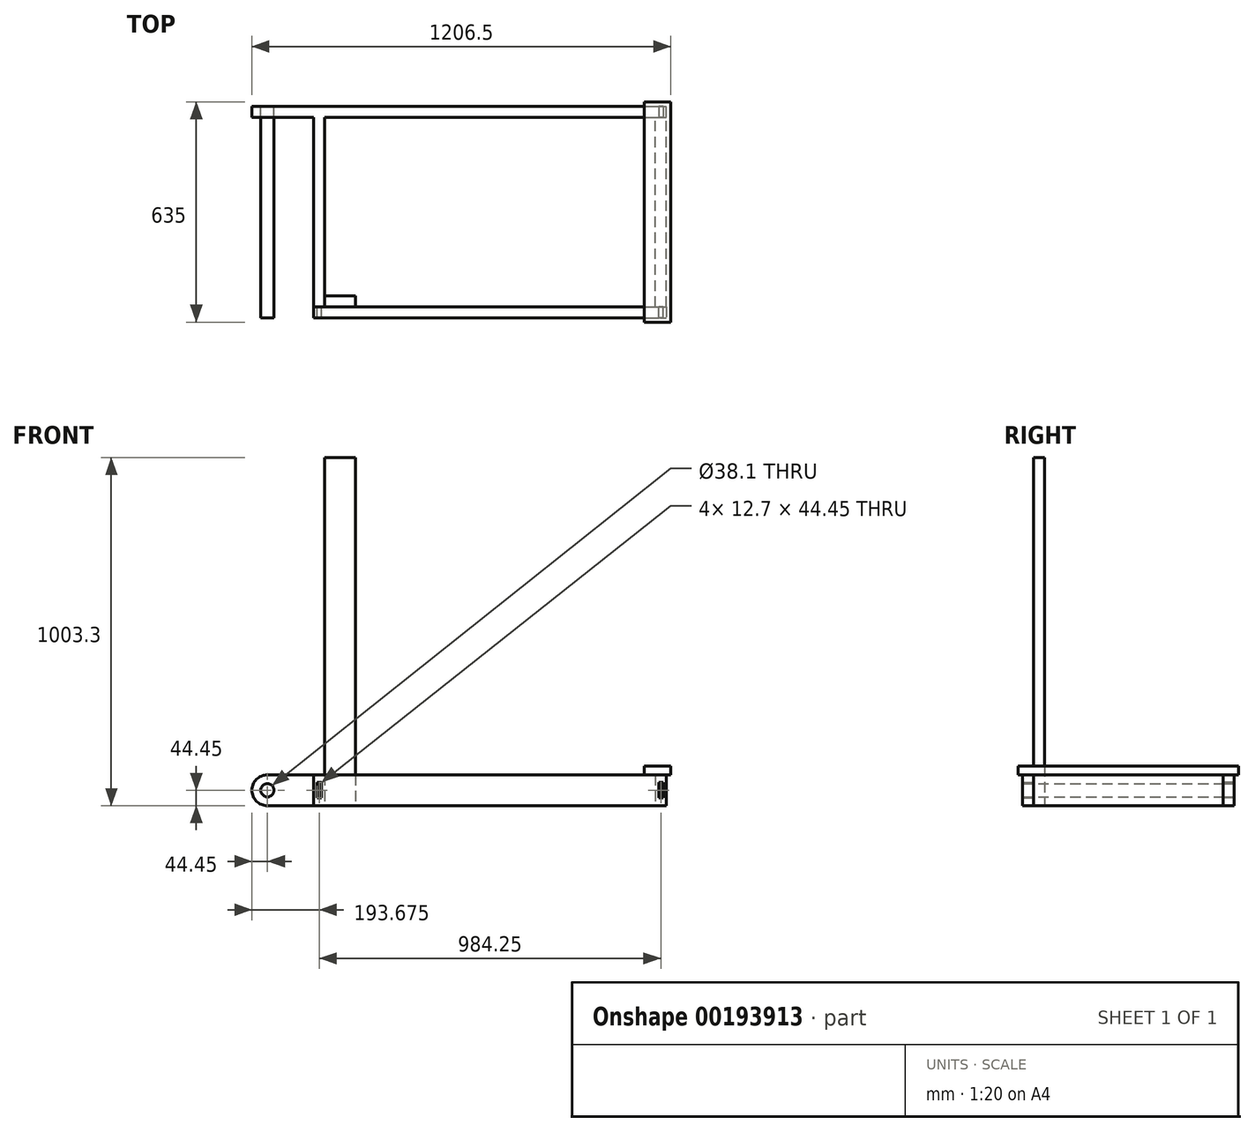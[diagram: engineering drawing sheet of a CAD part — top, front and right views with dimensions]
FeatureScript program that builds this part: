
annotation { "Feature Type Name" : "Feature", "Feature Type Description" : "" }
export const myFeature = defineFeature(function(context is Context, id is Id, definition is map)
    precondition{}
    {
        {
            var Q0;
            Q0=qCreatedBy(makeId("Top.planeOp"),FACE);
            var sketch = newSketch(context, id + "F0", { "sketchPlane" : qUnion([Q0])});
            skLineSegment(sketch, "E0.bottom", {"start": v(-508, 304.8) * mm, "end": v(508, 304.8) * mm});
            skLineSegment(sketch, "E0.top", {"start": v(-508, -304.8) * mm, "end": v(508, -304.8) * mm});
            skLineSegment(sketch, "E0.left", {"start": v(-508, 304.8) * mm, "end": v(-508, -304.8) * mm});
            skLineSegment(sketch, "E0.right", {"start": v(508, 304.8) * mm, "end": v(508, -304.8) * mm});
            skPoint(sketch, "E0.middle", {"position": v(0, 0) * mm});
            skLineSegment(sketch, "E1.0", {"start": v(-508, -273.05) * mm, "end": v(508, -273.05) * mm});
            skLineSegment(sketch, "E1.1", {"start": v(-476.25, 304.8) * mm, "end": v(-476.25, -304.8) * mm});
            skLineSegment(sketch, "E1.2", {"start": v(-508, 273.05) * mm, "end": v(508, 273.05) * mm});
            skLineSegment(sketch, "E1.3", {"start": v(476.25, 304.8) * mm, "end": v(476.25, -304.8) * mm});
            skSolve(sketch);
        }
        {
            var Q0;
            {var subQ4=sQuery(id+"F0.wireOp",EDGE,"E0.top");Q0=makeQuery(id+"F0.imprint","IMPRINT",FACE,{"disambiguationData":[TD([[makeQuery(id+"F0.imprint","IMPRINT",EDGE,{"derivedFrom":subQ4}),1.0]])]});}
            extrude(context, id + "F1", {"entities" : qUnion([Q0]), "oppositeDirection" : true, "depth" : 88.9 * mm});
        }
        {
            var Q0;
            Q0=makeQuery(id+"F1.opExtrude","SWEPT_FACE",FACE,{"disambiguationData":[OSD([sQuery(id+"F0.wireOp",EDGE,"E1.0")])]});
            var sketch = newSketch(context, id + "F2", { "sketchPlane" : qUnion([Q0])});
            skLineSegment(sketch, "E2", {"start": v(-476.25, 0) * mm, "end": v(-476.25, -88.9) * mm, "construction": true});
            skLineSegment(sketch, "E3", {"start": v(-476.25, 0) * mm, "end": v(-508, -88.9) * mm, "construction": true});
            skLineSegment(sketch, "E4.bottom", {"start": v(-498.47, -22.23) * mm, "end": v(-485.77, -22.23) * mm});
            skLineSegment(sketch, "E4.top", {"start": v(-498.47, -66.68) * mm, "end": v(-485.77, -66.68) * mm});
            skLineSegment(sketch, "E4.left", {"start": v(-498.47, -22.23) * mm, "end": v(-498.47, -66.68) * mm});
            skLineSegment(sketch, "E4.right", {"start": v(-485.77, -22.23) * mm, "end": v(-485.77, -66.68) * mm});
            skPoint(sketch, "E4.middle", {"position": v(-492.12, -44.45) * mm});
            skLineSegment(sketch, "E5", {"start": v(0, 0) * mm, "end": v(0, -88.9) * mm, "construction": true});
            skLineSegment(sketch, "E6.MirrorCS", {"start": v(485.77, -22.22) * mm, "end": v(485.77, -66.67) * mm});
            skLineSegment(sketch, "E7.MirrorCS", {"start": v(498.47, -22.22) * mm, "end": v(498.47, -66.67) * mm});
            skLineSegment(sketch, "E8.MirrorCS", {"start": v(498.47, -22.22) * mm, "end": v(485.77, -22.22) * mm});
            skLineSegment(sketch, "E9.MirrorCS", {"start": v(498.47, -66.67) * mm, "end": v(485.77, -66.67) * mm});
            skSolve(sketch);
        }
        {
            var Q0;
            Q0=makeQuery(id+"F2.imprint","IMPRINT",FACE,{"disambiguationData":[TD([[makeQuery(id+"F2.imprint","IMPRINT",EDGE,{"derivedFrom":sQuery(id+"F2.wireOp",EDGE,"E4.bottom")}),-1.0]])]});
            var Q1;
            Q1=makeQuery(id+"F2.imprint","IMPRINT",FACE,{"disambiguationData":[TD([[makeQuery(id+"F2.imprint","IMPRINT",EDGE,{"derivedFrom":sQuery(id+"F2.wireOp",EDGE,"E6.MirrorCS")}),1.0]])]});
            extrude(context, id + "F3", {"entities" : qUnion([Q0, Q1]), "operationType" : NewBodyOperationType.REMOVE, "endBound" : BoundingType.UP_TO_NEXT, "oppositeDirection" : true, "depth" : 25.4 * mm});
        }
        {
            var Q0;
            Q0=makeQuery(id+"F1.opExtrude","SWEPT_BODY",BODY,{"disambiguationData":[OSD([sQuery(id+"F0.wireOp",EDGE,"E0.top"),sQuery(id+"F0.wireOp",EDGE,"E0.left"),sQuery(id+"F0.wireOp",EDGE,"E0.right"),sQuery(id+"F0.wireOp",EDGE,"E1.0")])]});
            var Q1;
            Q1=qCreatedBy(makeId("Front.planeOp"),FACE);
            mirror(context, id + "F4", {"entities" : qUnion([Q0]), "mirrorPlane" : qUnion([Q1])});
        }
        {
            var Q0;
            {var subQ0=sQuery(id+"F0.wireOp",EDGE,"E0.right");var subQ1=sQuery(id+"F0.wireOp",EDGE,"E0.bottom");var subQ2=makeQuery(id+"F0.imprint","INTERSECT",VERTEX,{"derivedFrom":[subQ1,subQ0]});Q0=makeQuery(id+"F0.imprint","IMPRINT",FACE,{"disambiguationData":[TD([[makeQuery(id+"F0.imprint","IMPRINT",EDGE,{"disambiguationData":[TD([[subQ2,1.0]])],"derivedFrom":subQ1}),-1.0]])]});}
            var Q1;
            {var subQ0=sQuery(id+"F0.wireOp",EDGE,"E1.0");var subQ1=sQuery(id+"F0.wireOp",EDGE,"E0.right");var subQ2=makeQuery(id+"F0.imprint","INTERSECT",VERTEX,{"derivedFrom":[subQ1,subQ0]});Q1=makeQuery(id+"F0.imprint","IMPRINT",FACE,{"disambiguationData":[TD([[makeQuery(id+"F0.imprint","IMPRINT",EDGE,{"disambiguationData":[TD([[subQ2,1.0]])],"derivedFrom":subQ1}),-1.0]])]});}
            var Q2;
            {var subQ0=sQuery(id+"F0.wireOp",EDGE,"E0.right");var subQ1=sQuery(id+"F0.wireOp",EDGE,"E0.top");var subQ2=makeQuery(id+"F0.imprint","INTERSECT",VERTEX,{"derivedFrom":[subQ1,subQ0]});Q2=makeQuery(id+"F0.imprint","IMPRINT",FACE,{"disambiguationData":[TD([[makeQuery(id+"F0.imprint","IMPRINT",EDGE,{"disambiguationData":[TD([[subQ2,1.0]])],"derivedFrom":subQ1}),1.0]])]});}
            var Q3;
            Q3=makeQuery(id+"F1.opExtrude","CAP_FACE",FACE,{"disambiguationData":[OSD([sQuery(id+"F0.wireOp",EDGE,"E0.top"),sQuery(id+"F0.wireOp",EDGE,"E0.left"),sQuery(id+"F0.wireOp",EDGE,"E0.right"),sQuery(id+"F0.wireOp",EDGE,"E1.0")])],"isStart":false});
            extrude(context, id + "F5", {"entities" : qUnion([Q0, Q1, Q2]), "endBound" : BoundingType.UP_TO_SURFACE, "oppositeDirection" : true, "endBoundEntityFace" : qUnion([Q3]), "depth" : 25.4 * mm});
        }
        {
            var Q0;
            Q0=makeQuery(id+"F1.opExtrude","SWEPT_BODY",BODY,{"disambiguationData":[OSD([sQuery(id+"F0.wireOp",EDGE,"E0.top"),sQuery(id+"F0.wireOp",EDGE,"E0.left"),sQuery(id+"F0.wireOp",EDGE,"E0.right"),sQuery(id+"F0.wireOp",EDGE,"E1.0")])]});
            var Q1;
            Q1=makeQuery(id+"F4.opPattern","COPY",BODY,{"derivedFrom":makeQuery(id+"F1.opExtrude","SWEPT_BODY",BODY,{"disambiguationData":[OSD([sQuery(id+"F0.wireOp",EDGE,"E0.top"),sQuery(id+"F0.wireOp",EDGE,"E0.left"),sQuery(id+"F0.wireOp",EDGE,"E0.right"),sQuery(id+"F0.wireOp",EDGE,"E1.0")])]}),"instanceName":"1"});
            var Q2;
            Q2=makeQuery(id+"F5.opExtrude","SWEPT_BODY",BODY,{"disambiguationData":[OSD([sQuery(id+"F0.wireOp",EDGE,"E0.bottom"),sQuery(id+"F0.wireOp",EDGE,"E0.top"),sQuery(id+"F0.wireOp",EDGE,"E0.right"),sQuery(id+"F0.wireOp",EDGE,"E1.3")])]});
            booleanBodies(context, id + "F6", {"operationType" : BooleanOperationType.SUBTRACTION, "tools" : qUnion([Q0, Q1]), "targets" : qUnion([Q2]), "keepTools" : true});
        }
        {
            var Q0;
            Q0=makeQuery(id+"F5.opExtrude","SWEPT_BODY",BODY,{"disambiguationData":[OSD([sQuery(id+"F0.wireOp",EDGE,"E0.bottom"),sQuery(id+"F0.wireOp",EDGE,"E0.top"),sQuery(id+"F0.wireOp",EDGE,"E0.right"),sQuery(id+"F0.wireOp",EDGE,"E1.3")])]});
            var Q1;
            Q1=qCreatedBy(makeId("Right.planeOp"),FACE);
            mirror(context, id + "F7", {"entities" : qUnion([Q0]), "mirrorPlane" : qUnion([Q1])});
        }
        {
            var Q0;
            {var subQ0=sQuery(id+"F0.wireOp",EDGE,"E0.left");var subQ1=sQuery(id+"F0.wireOp",EDGE,"E0.top");var subQ2=makeQuery(id+"F0.imprint","INTERSECT",VERTEX,{"derivedFrom":[subQ1,subQ0]});Q0=makeQuery(id+"F0.imprint","IMPRINT",FACE,{"disambiguationData":[TD([[makeQuery(id+"F0.imprint","IMPRINT",EDGE,{"disambiguationData":[TD([[subQ2,-1.0]])],"derivedFrom":subQ1}),1.0]])]});}
            var sketch = newSketch(context, id + "F8", { "sketchPlane" : qUnion([Q0])});
            skLineSegment(sketch, "E10.0", {"start": v(-476.25, 304.8) * mm, "end": v(-476.25, -304.8) * mm, "construction": true});
            skLineSegment(sketch, "E11.0", {"start": v(-508, -273.05) * mm, "end": v(508, -273.05) * mm, "construction": true});
            skLineSegment(sketch, "E12.bottom", {"start": v(-476.25, -273.05) * mm, "end": v(-387.35, -273.05) * mm});
            skLineSegment(sketch, "E12.top", {"start": v(-476.25, -241.3) * mm, "end": v(-387.35, -241.3) * mm});
            skLineSegment(sketch, "E12.left", {"start": v(-476.25, -273.05) * mm, "end": v(-476.25, -241.3) * mm});
            skLineSegment(sketch, "E12.right", {"start": v(-387.35, -273.05) * mm, "end": v(-387.35, -241.3) * mm});
            skSolve(sketch);
        }
        {
            var Q0;
            Q0 = qSketchRegion(id + "F8", true);
            var Q1;
            Q1=makeQuery(id+"F1.opExtrude","CAP_FACE",FACE,{"disambiguationData":[OSD([sQuery(id+"F0.wireOp",EDGE,"E0.top"),sQuery(id+"F0.wireOp",EDGE,"E0.left"),sQuery(id+"F0.wireOp",EDGE,"E0.right"),sQuery(id+"F0.wireOp",EDGE,"E1.0")])],"isStart":false});
            extrude(context, id + "F9", {"entities" : qUnion([Q0]), "depth" : 914.4 * mm, "hasSecondDirection" : true, "secondDirectionBound" : SecondDirectionBoundingType.UP_TO_SURFACE, "secondDirectionOppositeDirection" : true, "secondDirectionBoundEntityFace" : qUnion([Q1]), "secondDirectionDepth" : 25.4 * mm});
        }
        {
            var Q0;
            Q0=makeQuery(id+"F4.opPattern","COPY",FACE,{"derivedFrom":makeQuery(id+"F1.opExtrude","SWEPT_FACE",FACE,{"disambiguationData":[OSD([sQuery(id+"F0.wireOp",EDGE,"E0.left")])]}),"instanceName":"1"});
            var sketch = newSketch(context, id + "F10", { "sketchPlane" : qUnion([Q0])});
            skLineSegment(sketch, "E13.0.0", {"start": v(-273.05, 0) * mm, "end": v(-304.8, 0) * mm});
            skLineSegment(sketch, "E13.0.1", {"start": v(-304.8, 0) * mm, "end": v(-304.8, -88.9) * mm});
            skLineSegment(sketch, "E13.0.2", {"start": v(-304.8, -88.9) * mm, "end": v(-273.05, -88.9) * mm});
            skLineSegment(sketch, "E13.0.3", {"start": v(-273.05, -88.9) * mm, "end": v(-273.05, 0) * mm});
            skSolve(sketch);
        }
        {
            var Q0;
            Q0 = qSketchRegion(id + "F10", true);
            extrude(context, id + "F11", {"entities" : qUnion([Q0]), "operationType" : NewBodyOperationType.ADD, "depth" : 177.8 * mm});
        }
        {
            var Q0;
            Q0=makeQuery(id+"F11.boolean.opBoolean","MERGE",FACE,{"derivedFrom":[makeQuery(id+"F4.opPattern","COPY",FACE,{"derivedFrom":makeQuery(id+"F1.opExtrude","SWEPT_FACE",FACE,{"disambiguationData":[OSD([sQuery(id+"F0.wireOp",EDGE,"E0.top")])]}),"instanceName":"1"}),makeQuery(id+"F11.opExtrude","SWEPT_FACE",FACE,{"disambiguationData":[OSD([sQuery(id+"F10.wireOp",EDGE,"E13.0.1")])]})]});
            var sketch = newSketch(context, id + "F12", { "sketchPlane" : qUnion([Q0])});
            skLineSegment(sketch, "E14.bottom", {"start": v(685.8, -88.9) * mm, "end": v(596.9, -88.9) * mm});
            skLineSegment(sketch, "E14.top", {"start": v(685.8, 0) * mm, "end": v(596.9, 0) * mm});
            skLineSegment(sketch, "E14.left", {"start": v(685.8, -88.9) * mm, "end": v(685.8, 0) * mm});
            skLineSegment(sketch, "E14.right", {"start": v(596.9, -88.9) * mm, "end": v(596.9, 0) * mm, "construction": true});
            skLineSegment(sketch, "E15", {"start": v(685.8, -88.9) * mm, "end": v(596.9, 0) * mm, "construction": true});
            skCircle(sketch, "E16", {"center": v(641.35, -44.45) * mm, "radius": 44.45 * mm});
            skCircle(sketch, "E17", {"center": v(641.35, -44.45) * mm, "radius": 19.05 * mm});
            skSolve(sketch);
        }
        {
            var Q0;
            {var subQ0=sQuery(id+"F12.wireOp",EDGE,"E14.left");var subQ1=sQuery(id+"F12.wireOp",EDGE,"E14.bottom");var subQ2=makeQuery(id+"F12.imprint","INTERSECT",VERTEX,{"derivedFrom":[subQ1,subQ0]});Q0=makeQuery(id+"F12.imprint","IMPRINT",FACE,{"disambiguationData":[TD([[makeQuery(id+"F12.imprint","IMPRINT",EDGE,{"disambiguationData":[TD([[subQ2,-1.0]])],"derivedFrom":subQ1}),-1.0]])]});}
            var Q1;
            {var subQ0=sQuery(id+"F12.wireOp",EDGE,"E14.left");var subQ1=sQuery(id+"F12.wireOp",EDGE,"E14.top");var subQ2=makeQuery(id+"F12.imprint","INTERSECT",VERTEX,{"derivedFrom":[subQ1,subQ0]});Q1=makeQuery(id+"F12.imprint","IMPRINT",FACE,{"disambiguationData":[TD([[makeQuery(id+"F12.imprint","IMPRINT",EDGE,{"disambiguationData":[TD([[subQ2,-1.0]])],"derivedFrom":subQ1}),1.0]])]});}
            var Q2;
            Q2=makeQuery(id+"F12.imprint","IMPRINT",FACE,{"disambiguationData":[TD([[makeQuery(id+"F12.imprint","IMPRINT",EDGE,{"derivedFrom":sQuery(id+"F12.wireOp",EDGE,"E17")}),1.0]])]});
            extrude(context, id + "F13", {"entities" : qUnion([Q0, Q1, Q2]), "operationType" : NewBodyOperationType.REMOVE, "endBound" : BoundingType.UP_TO_NEXT, "oppositeDirection" : true, "depth" : 25.4 * mm});
        }
        {
            var Q0;
            Q0=makeQuery(id+"F12.imprint","IMPRINT",FACE,{"disambiguationData":[TD([[makeQuery(id+"F12.imprint","IMPRINT",EDGE,{"derivedFrom":sQuery(id+"F12.wireOp",EDGE,"E17")}),1.0]])]});
            var Q1;
            Q1=sQuery(id+"F12.wireOp",EDGE,"E17");
            var Q2;
            Q2=makeQuery(id+"F1.opExtrude","SWEPT_FACE",FACE,{"disambiguationData":[OSD([sQuery(id+"F0.wireOp",EDGE,"E0.top")])]});
            extrude(context, id + "F14", {"entities" : qUnion([Q0]), "surfaceEntities" : qUnion([Q1]), "endBound" : BoundingType.UP_TO_SURFACE, "oppositeDirection" : true, "endBoundEntityFace" : qUnion([Q2]), "depth" : 805.18 * mm});
        }
        {
            var Q0;
            Q0=qCreatedBy(makeId("Top.planeOp"),FACE);
            var sketch = newSketch(context, id + "F15", { "sketchPlane" : qUnion([Q0])});
            skPoint(sketch, "E18.0", {"position": v(508, -304.8) * mm});
            skLineSegment(sketch, "E18.1", {"start": v(-641.35, 304.8) * mm, "end": v(508, 304.8) * mm, "construction": true});
            skLineSegment(sketch, "E19.bottom", {"start": v(508, -304.8) * mm, "end": v(457.2, -304.8) * mm, "construction": true});
            skLineSegment(sketch, "E19.top", {"start": v(508, 304.8) * mm, "end": v(457.2, 304.8) * mm});
            skLineSegment(sketch, "E19.left", {"start": v(508, -304.8) * mm, "end": v(508, 304.8) * mm, "construction": true});
            skLineSegment(sketch, "E19.right", {"start": v(457.2, -304.8) * mm, "end": v(457.2, 304.8) * mm, "construction": true});
            skLineSegment(sketch, "E20.0", {"start": v(520.7, -317.5) * mm, "end": v(520.7, 317.5) * mm});
            skLineSegment(sketch, "E20.1", {"start": v(520.7, -317.5) * mm, "end": v(444.5, -317.5) * mm});
            skLineSegment(sketch, "E20.2", {"start": v(444.5, -317.5) * mm, "end": v(444.5, 317.5) * mm});
            skLineSegment(sketch, "E20.3", {"start": v(520.7, 317.5) * mm, "end": v(444.5, 317.5) * mm});
            skSolve(sketch);
        }
        {
            var Q0;
            Q0 = qSketchRegion(id + "F15", true);
            extrude(context, id + "F16", {"entities" : qUnion([Q0]), "depth" : 25.4 * mm});
        }
    });
